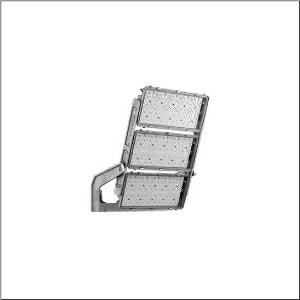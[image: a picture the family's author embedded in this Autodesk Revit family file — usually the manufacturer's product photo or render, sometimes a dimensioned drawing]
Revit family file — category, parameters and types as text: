
# Revit family: floodlight_fl_11_maxi_pro_remote___pl64_5xa779425v01aa_e912
name_source: partatom
category: Lighting Fixtures
units: mm (PartAtom-declared; Revit-internal decimal feet)

## family parameters
Cut with Voids When Loaded = No
Host = Face
Light Source = No
Part Type = Normal
Room Calculation Point = No
Round Connector Dimension = Use Diameter
Shared = No

## types (1)
- --- (1 x LED, 206660 lm, 1539.3 W, 3000K)
    Apparent Load = 1539 VA
    CIE Flux Codes = 28 79 98 100 100
    Color Rendering = 70
    Color Temperature = 3000K
    Default Elevation = 1800 mm
    Description = Floodlight FL 11  maxi  pro Remote floodlight; light control with lens of PMMA; cover panel of toughened safety glass, transparent; light distribution: PL64, asymmetric direct distribution, LEDcolour temperature: 3000K, rated luminous flux: 206.660lm, colour rendering: CRI > 70, light colour: 730; luminous efficacy: 134lm/W; brightness control: DALI 2 (1 DALI address); with terminal, 8-pole, max. 2.5mm², mains connection: 220..240V/380..400V AC, 50/60Hz, surge voltage resistance: line to ground: 10kV, ECG replaceable separately, no afterglow with DALI off / DMX off command, LED unit replaceable without ESD environment, dustproof LED module, dimming range 10..100%; 1539W floodlight with 2x LED unit of diecast aluminium, coated grey; length: 713mm / width: 651mm / height: 338mm; mounting bracket, of diecast aluminium, uncoated, natural, equipment: Power, protection rating (complete): IP66; insulation class (complete): insulation class I (protective earthing); certification: CE, ENEC, VDE; ball protection: ball impact resistance with accessories, impact resistance: IK07; only for outdoor installations, rated ambient temperature 10°C, permissible operating ambient temperature: -40..+30°C, permissible storage temperature: -40..+85°Cpackaging unit: 1 piece

Light Distribution: PL64
    Height = 320 mm
    Lamp = 1 x LED
    Lamp Light Flux = 206660 lm
    Lamp Power = 1539.3 W
    Lamp count = 1
    Length = 1002 mm
    Luminous efficacy = 134 lm/W
    Manufacturer = Siteco
    ModVariant = No
    Model = 5XA779425V01AA
    Mounting Place = Ceiling
    Mounting Type = Surface mounted
    Number of Poles = 1
    OnlyDefault = Yes
    Power Factor = 1
    Product Name = Floodlight FL 11 maxi pro Remote | PL64
    Product group = floodlight | ceiling mounted
    ProductGroupID = 301
    Protection Class = Protection class I
    Protection Degree = IP 66
    RLX_Detail_Level = 1
    RLX_Emergency_Light_Flux = 0 lm
    RLX_Emergency_Type = 0
    RLX_Emergency_Type_DB = No
    RlxData = <blob elided: 52709 chars, md5=7c7d9e01>
    Socket = socket
    Standby Power = 0 W
    System Light Flux = 206660 lm
    System Power = 1539 W
    Type Comments = factory setting: luminous flux: 100 % | dim-lin: 254 | 1080 mA
    Type Image = l_1349141.jpg
    URL = http://relux.com
    VarID = @adj_102984
    Voltage = 0 V
    Weight = 0.00 kg
    Width = 655 mm

## geometry (parser evidence)
native form markers: Blend x4, Sweep x14
no freeform markers — native parametric forms only
